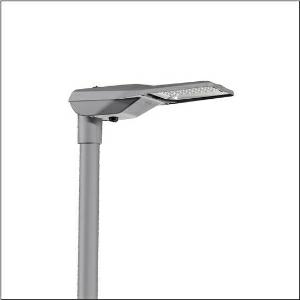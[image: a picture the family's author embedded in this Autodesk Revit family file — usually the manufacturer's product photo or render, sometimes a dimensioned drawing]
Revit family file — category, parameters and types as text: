
# Revit family: streetlight_sl_21_iq_mini___st1_0a_5xe2d61y08jb_b42a
name_source: partatom
category: Lighting Fixtures
units: mm (PartAtom-declared; Revit-internal decimal feet)

## family parameters
Cut with Voids When Loaded = No
Host = Face
Light Source = No
Part Type = Normal
Room Calculation Point = No
Round Connector Dimension = Use Diameter
Shared = No

## types (1)
- --- (1 x LED, 9730 lm, 72.5 W, 2700K)
    Apparent Load = 73 VA
    CIE Flux Codes = 40 73 97 100 100
    Color Rendering = 70
    Color Temperature = 2700K
    Default Elevation = 1800 mm
    Description = Streetlight SL 21 iQ mini, mast luminaire, primary light control with lens, of PMMA, primary optical cover: cover, of toughened safety glass, transparent, light distribution: ST1.0a, light emission: direct distribution, primary light characteristic: asymmetric, installation type: post-top, side-entry, LED, High Power LED, rated luminous flux: 9.730lm, luminous efficacy: 134lm/W, light colour: 727, colour temperature: 2700K, control gear: iQ-Street Remote, D4i with power reduction, control: pre-setting: logarithmic dimming characteristic, Street-Remote, Auto-Match, Temp-Guard, Lumen-Switch, Night-Set, Smart-Wire, Light-Fading, Desk-Remote (wireless, voltage-free reading and setting of iQ features in the workshop via application-optimized NFC function/RFID function), optimised constant luminous flux control (CLO 2.0), mains connection: 220..240V, AC, 50/60Hz, start of lifetime: 73W, end of service life: 76W, reduction: 33W, luminaire housing, of diecast aluminium, powder-coated, Siteco® metallic grey (DB 702S), corrosivity category C5 mid according to DIN EN ISO 12944, please order mast flange separately, inclination adjustable: 0°, 5°, 10°, 15°, sealing non-destructively replaceable, multi-level sealing system, length: 628mm, width: 235mm, height: 110mm, mast flange for spigot size: 42mm (side-entry): 5XC10008XM4, 60/48mm (side-entry/post-top): 5XC10108XM2, 76/60mm (side-entry/post-top): 5XC10108XM1, mounting height: 4..8m, Smart Interface below and above, protection rating (complete): IP66, insulation class (complete): insulation class II (safety insulation), certification: CE, ENEC, ENEC+, VDE, impact resistance: IK10, permissible operating ambient temperature for outdoor applications: -40..+50°C, standard-compliant lighting for roads and squares, packaging unit: 1 piece

Light Distribution: ST1.0a
    Height = 110 mm
    Lamp = 1 x LED
    Lamp Light Flux = 9730 lm
    Lamp Power = 72.5 W
    Lamp count = 1
    Length = 625 mm
    Luminous efficacy = 134 lm/W
    Manufacturer = Siteco
    ModVariant = No
    Model = 5XE2D61Y08JB
    Number of Poles = 1
    OnlyDefault = Yes
    Power Factor = 1
    Product Name = Streetlight SL 21 iQ mini | ST1.0a
    Product group = mast luminaire | pylon top
    ProductGroupID = 6100
    Protection Class = Protection class II
    Protection Degree = IP 66
    RLX_Detail_Level = 1
    RLX_Emergency_Light_Flux = 0 lm
    RLX_Emergency_Type = 0
    RLX_Emergency_Type_DB = No
    RlxData = <blob elided: 26645 chars, md5=feb452f0>
    Socket = socket
    Standby Power = 0 W
    System Light Flux = 9730 lm
    System Power = 73 W
    Type Comments = factory setting: luminous flux: 100 % | dim-lin: 254 | 755 mA
    Type Image = l_1003514.jpg
    URL = http://relux.com
    VarID = @adj_114110
    Voltage = 0 V
    Weight = 0.00 kg
    Width = 234 mm

## geometry (parser evidence)
native form markers: Blend x4, Sweep x11
no freeform markers — native parametric forms only
